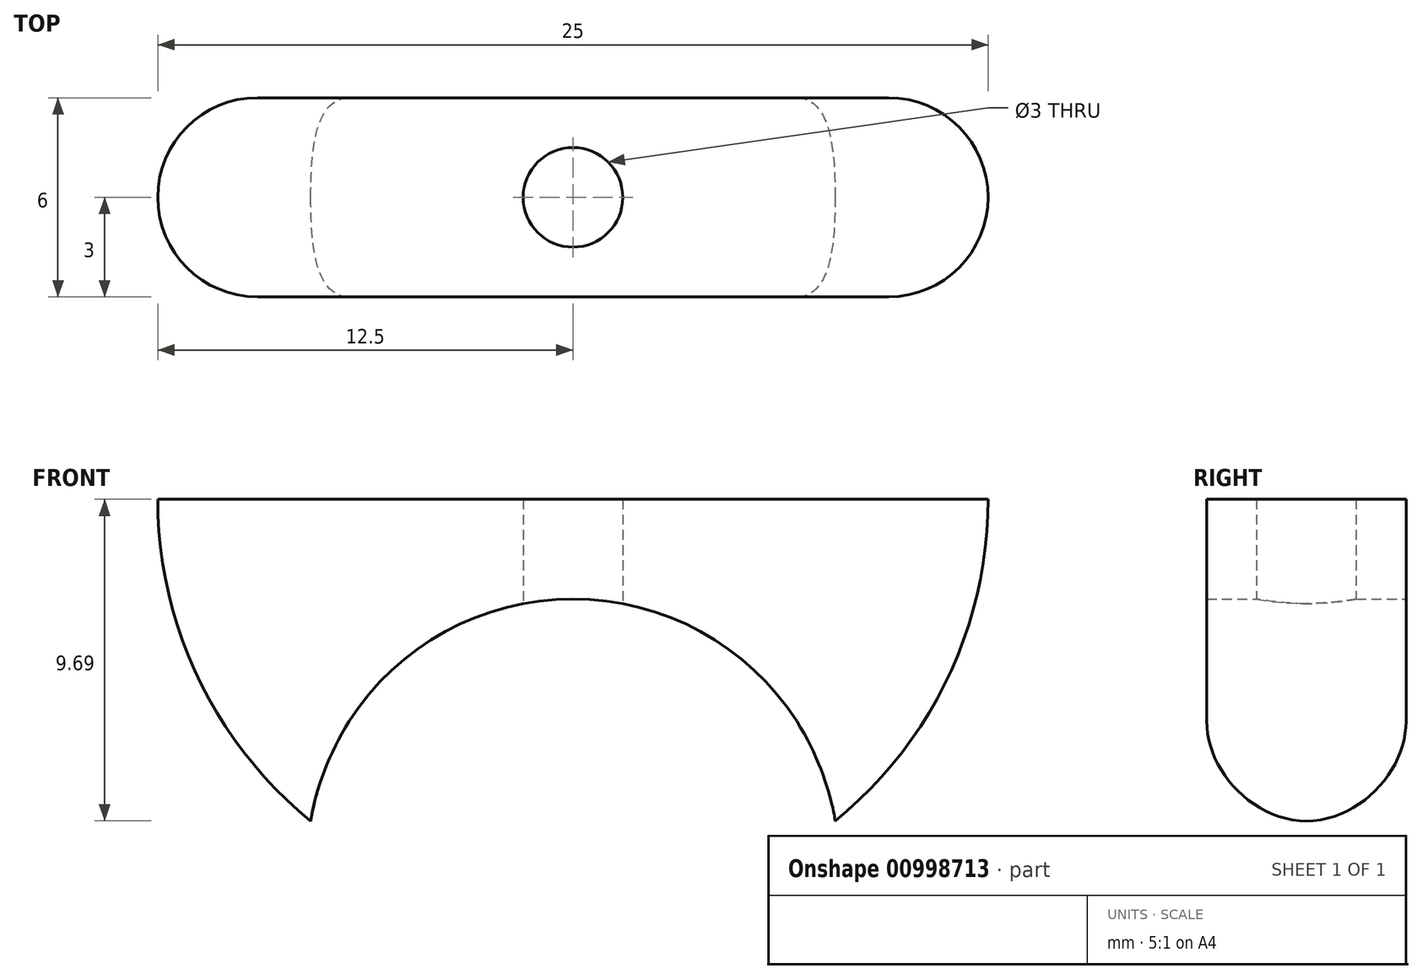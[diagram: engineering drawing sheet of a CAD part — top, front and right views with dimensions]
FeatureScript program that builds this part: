
annotation { "Feature Type Name" : "Feature", "Feature Type Description" : "" }
export const myFeature = defineFeature(function(context is Context, id is Id, definition is map)
    precondition{}
    {
        {
            var Q0;
            Q0=qCreatedBy(makeId("Front.planeOp"),FACE);
            var sketch = newSketch(context, id + "F0", { "sketchPlane" : qUnion([Q0])});
            skLineSegment(sketch, "E0", {"start": v(-12.5, 11) * mm, "end": v(12.5, 11) * mm});
            skLineSegment(sketch, "E1", {"start": v(0, 28.64) * mm, "end": v(0, -29.65) * mm, "construction": true});
            skPoint(sketch, "E2.start.orphan", {"position": v(-8, 0) * mm});
            skPoint(sketch, "E3.start.orphan", {"position": v(8, 0) * mm});
            skArc(sketch, "E4", {"start": v(8, 0) * mm, "mid": v(0, 8) * mm, "end": v(-8, 0) * mm});
            skArc(sketch, "E5", {"start": v(-12.5, 11) * mm, "mid": v(-11.29, 5.63) * mm, "end": v(-7.9, 1.3) * mm});
            skArc(sketch, "E6.trimOffspring", {"start": v(7.9, 1.3) * mm, "mid": v(11.29, 5.63) * mm, "end": v(12.5, 11) * mm});
            skSolve(sketch);
        }
        {
            var Q0;
            Q0=makeQuery(id+"F0.imprint","IMPRINT",FACE,{"disambiguationData":[TD([[makeQuery(id+"F0.imprint","IMPRINT",EDGE,{"derivedFrom":sQuery(id+"F0.wireOp",EDGE,"qkrqzse2-mHjl-FPVe-h8ui-Bncq6iStuv0d")}),-1.0]])]});
            var Q1;
            Q1=makeQuery(id+"F0.imprint","IMPRINT",FACE,{"disambiguationData":[TD([[makeQuery(id+"F0.imprint","IMPRINT",EDGE,{"derivedFrom":sQuery(id+"F0.wireOp",EDGE,"E0")}),-1.0]])]});
            extrude(context, id + "F1", {"entities" : qUnion([Q0, Q1]), "endBound" : BoundingType.SYMMETRIC, "depth" : 6 * mm, "offsetDistance" : 25.4 * mm});
        }
        {
            var Q0;
            Q0=makeQuery(id+"F1.opExtrude","CAP_EDGE",EDGE,{"disambiguationData":[OSD([sQuery(id+"F0.wireOp",EDGE,"E5")])],"isStart":false});
            var Q1;
            Q1=makeQuery(id+"F1.opExtrude","CAP_EDGE",EDGE,{"disambiguationData":[OSD([sQuery(id+"F0.wireOp",EDGE,"E5")])],"isStart":true});
            var Q2;
            Q2=makeQuery(id+"F1.opExtrude","CAP_EDGE",EDGE,{"disambiguationData":[OSD([sQuery(id+"F0.wireOp",EDGE,"E6.trimOffspring")])],"isStart":false});
            var Q3;
            Q3=makeQuery(id+"F1.opExtrude","CAP_EDGE",EDGE,{"disambiguationData":[OSD([sQuery(id+"F0.wireOp",EDGE,"E6.trimOffspring")])],"isStart":true});
            fillet(context, id + "F2", {"entities" : qUnion([Q0, Q1, Q2, Q3]), "radius" : 3 * mm, "tangentPropagation" : true, "allowEdgeOverflow" : false});
        }
        {
            var Q0;
            Q0=qCreatedBy(makeId("Top.planeOp"),FACE);
            var sketch = newSketch(context, id + "F3", { "sketchPlane" : qUnion([Q0])});
            skCircle(sketch, "E7", {"center": v(0, 0) * mm, "radius": 1.5 * mm});
            skSolve(sketch);
        }
        {
            var Q0;
            Q0=makeQuery(id+"F3.imprint","IMPRINT",FACE,{"disambiguationData":[TD([[makeQuery(id+"F3.imprint","IMPRINT",EDGE,{"derivedFrom":sQuery(id+"F3.wireOp",EDGE,"E7")}),1.0]])]});
            extrude(context, id + "F4", {"entities" : qUnion([Q0]), "operationType" : NewBodyOperationType.REMOVE, "endBound" : BoundingType.THROUGH_ALL, "depth" : 25 * mm, "offsetDistance" : 25 * mm});
        }
    });
